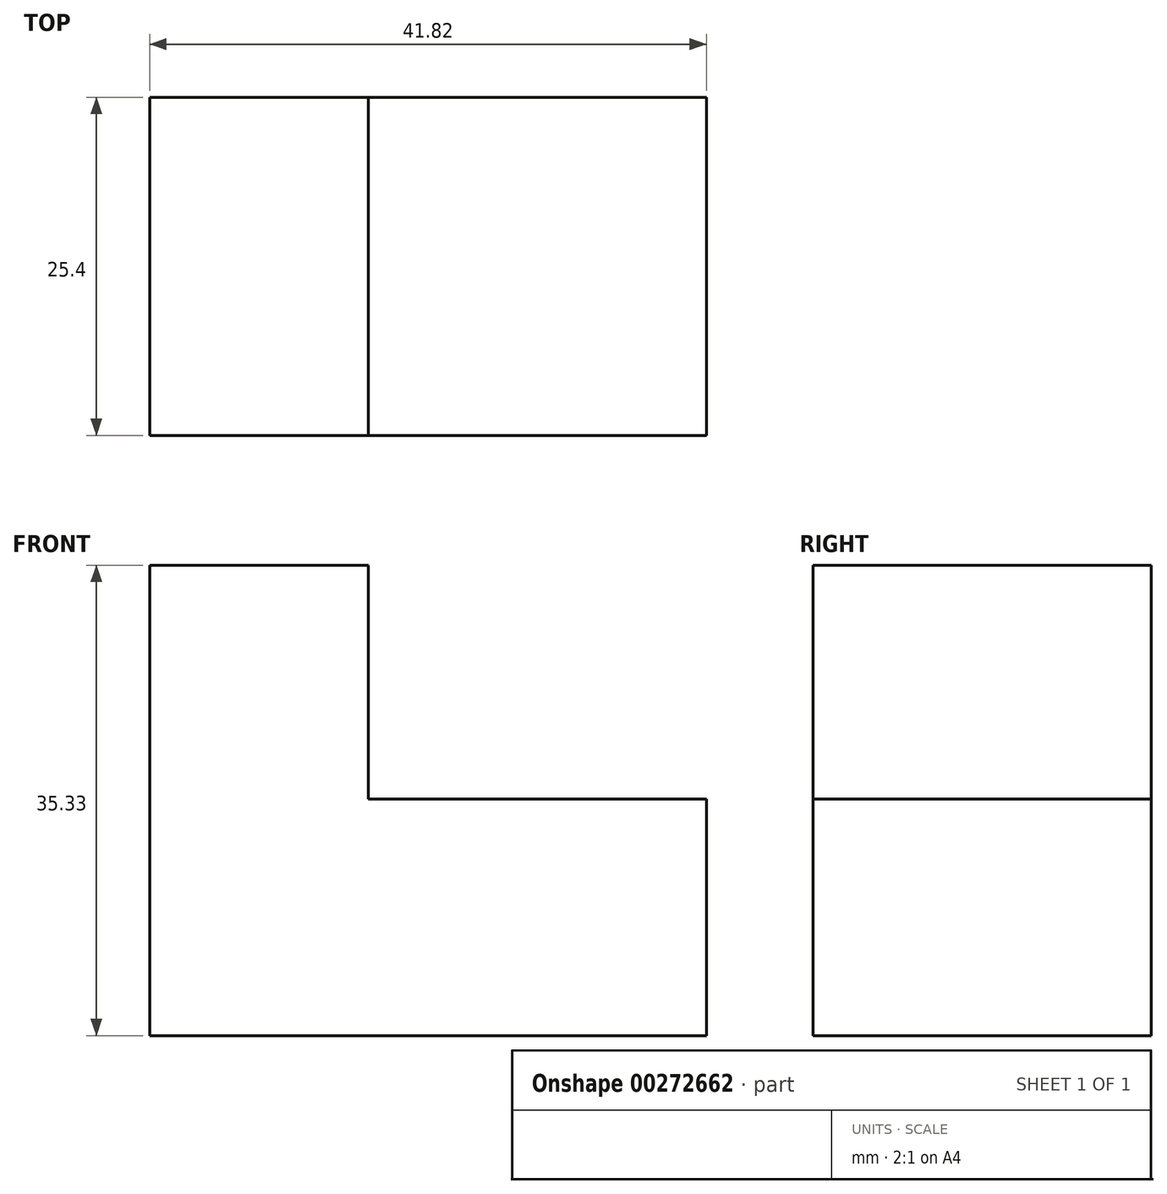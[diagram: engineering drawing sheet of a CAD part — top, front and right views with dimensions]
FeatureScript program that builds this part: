
annotation { "Feature Type Name" : "Feature", "Feature Type Description" : "" }
export const myFeature = defineFeature(function(context is Context, id is Id, definition is map)
    precondition{}
    {
        {
            var Q0;
            Q0=qCreatedBy(makeId("Front.planeOp"),FACE);
            var sketch = newSketch(context, id + "F0", { "sketchPlane" : qUnion([Q0])});
            skLineSegment(sketch, "E0", {"start": v(0, 0) * mm, "end": v(-41.82, 0) * mm});
            skLineSegment(sketch, "E1", {"start": v(-41.82, 0) * mm, "end": v(-41.82, 35.33) * mm});
            skLineSegment(sketch, "E2", {"start": v(-41.82, 35.33) * mm, "end": v(-25.4, 35.33) * mm});
            skLineSegment(sketch, "E3", {"start": v(-25.4, 35.33) * mm, "end": v(-25.4, 17.76) * mm});
            skLineSegment(sketch, "E4", {"start": v(-25.4, 17.76) * mm, "end": v(0, 17.76) * mm});
            skLineSegment(sketch, "E5", {"start": v(0, 17.76) * mm, "end": v(0, 0) * mm});
            skSolve(sketch);
        }
        {
            var Q0;
            Q0 = qSketchRegion(id + "F0", true);
            extrude(context, id + "F1", {"entities" : qUnion([Q0]), "depth" : 25.4 * mm});
        }
    });
